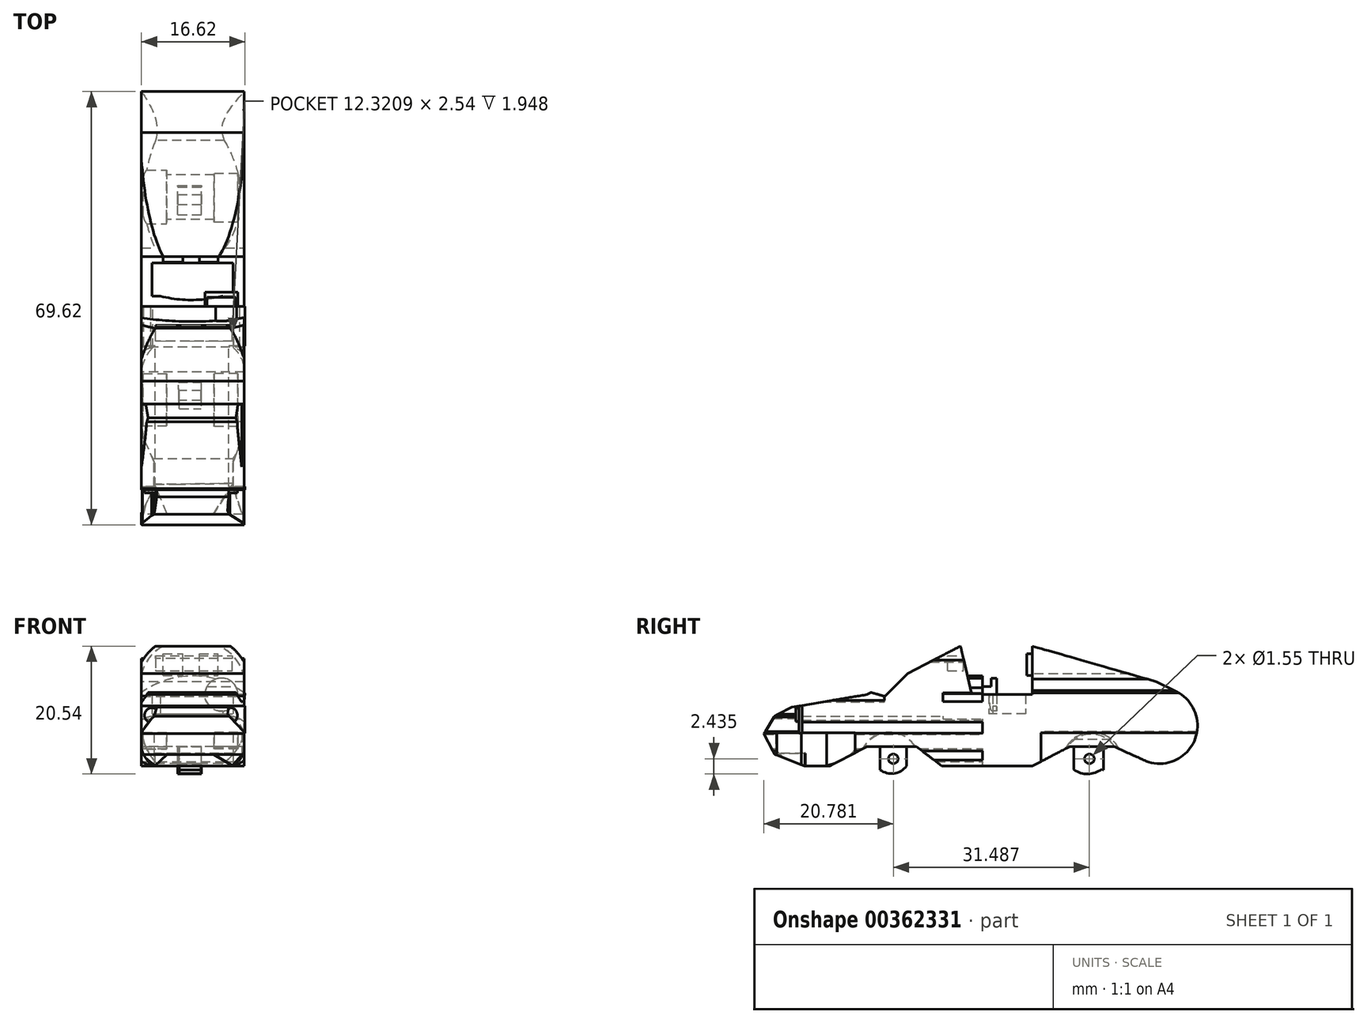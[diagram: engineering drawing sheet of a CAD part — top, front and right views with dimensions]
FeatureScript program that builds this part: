
annotation { "Feature Type Name" : "Feature", "Feature Type Description" : "" }
export const myFeature = defineFeature(function(context is Context, id is Id, definition is map)
    precondition{}
    {
        {
            var Q0;
            Q0=qCreatedBy(makeId("Right.planeOp"),FACE);
            var sketch = newSketch(context, id + "F0", { "sketchPlane" : qUnion([Q0])});
            skArc(sketch, "E0", {"start": v(26.7, 3.42) * mm, "mid": v(34.12, 7.05) * mm, "end": v(31.15, 14.76) * mm});
            skLineSegment(sketch, "E1", {"start": v(31.15, 14.76) * mm, "end": v(27.94, 16.36) * mm});
            skLineSegment(sketch, "E2", {"start": v(27.94, 16.36) * mm, "end": v(8.03, 22.06) * mm});
            skLineSegment(sketch, "E3", {"start": v(8.03, 22.06) * mm, "end": v(8.03, 14.28) * mm});
            skLineSegment(sketch, "E4", {"start": v(8.03, 14.28) * mm, "end": v(-1.74, 14.28) * mm});
            skLineSegment(sketch, "E5", {"start": v(-1.74, 14.28) * mm, "end": v(-3.5, 22.06) * mm});
            skLineSegment(sketch, "E6", {"start": v(-3.5, 22.06) * mm, "end": v(-18.55, 14.28) * mm});
            skLineSegment(sketch, "E7", {"start": v(-18.55, 14.28) * mm, "end": v(-1.74, 14.28) * mm});
            skLineSegment(sketch, "E8", {"start": v(-18.55, 14.28) * mm, "end": v(-30.58, 12.25) * mm});
            skLineSegment(sketch, "E9", {"start": v(-30.58, 12.25) * mm, "end": v(-33.36, 10.81) * mm});
            skLineSegment(sketch, "E10", {"start": v(-33.36, 10.81) * mm, "end": v(-35.08, 7.98) * mm});
            skLineSegment(sketch, "E11", {"start": v(-35.08, 7.98) * mm, "end": v(-33.36, 4.67) * mm});
            skLineSegment(sketch, "E12", {"start": v(-33.36, 4.67) * mm, "end": v(-28.56, 2.8) * mm});
            skLineSegment(sketch, "E13", {"start": v(-28.56, 2.8) * mm, "end": v(-24.5, 2.8) * mm});
            skLineSegment(sketch, "E14", {"start": v(-24.5, 2.8) * mm, "end": v(-18.55, 5.89) * mm});
            skLineSegment(sketch, "E15", {"start": v(-18.55, 5.89) * mm, "end": v(-10.56, 5.89) * mm});
            skLineSegment(sketch, "E16", {"start": v(-10.56, 5.89) * mm, "end": v(-6.5, 2.8) * mm});
            skLineSegment(sketch, "E17", {"start": v(-6.5, 2.8) * mm, "end": v(8.03, 2.8) * mm});
            skLineSegment(sketch, "E18", {"start": v(8.03, 2.8) * mm, "end": v(13.99, 5.89) * mm});
            skLineSegment(sketch, "E19", {"start": v(13.99, 5.89) * mm, "end": v(21.18, 5.89) * mm});
            skLineSegment(sketch, "E20", {"start": v(21.18, 5.89) * mm, "end": v(26.7, 3.42) * mm});
            skSolve(sketch);
        }
        {
            var Q0;
            Q0 = qSketchRegion(id + "F0", true);
            extrude(context, id + "F1", {"entities" : qUnion([Q0]), "depth" : 16.5 * mm});
        }
        {
            var Q0;
            Q0=qCreatedBy(makeId("Top.planeOp"),FACE);
            cPlane(context, id + "F2", {"entities" : qUnion([Q0]), "cplaneType" : CPlaneType.OFFSET, "offset" : 8.38 * mm, "width" : 152.4 * mm, "height" : 152.4 * mm});
        }
        {
            var Q0;
            Q0=qCreatedBy(makeId("Right.planeOp"),FACE);
            cPlane(context, id + "F3", {"entities" : qUnion([Q0]), "cplaneType" : CPlaneType.OFFSET, "offset" : 7.87 * mm, "width" : 152.4 * mm, "height" : 152.4 * mm});
        }
        {
            var Q0;
            Q0=qCreatedBy(makeId("Right.planeOp"),FACE);
            cPlane(context, id + "F4", {"entities" : qUnion([Q0]), "cplaneType" : CPlaneType.OFFSET, "offset" : 11.68 * mm, "width" : 152.4 * mm, "height" : 152.4 * mm});
        }
        {
            var Q0;
            Q0=qCreatedBy(id+"F3.planeOp",FACE);
            cPlane(context, id + "F5", {"entities" : qUnion([Q0]), "cplaneType" : CPlaneType.OFFSET, "offset" : 3.8 * mm, "oppositeDirection" : true, "width" : 152.4 * mm, "height" : 152.4 * mm});
        }
        {
            var Q0;
            Q0=qCreatedBy(id+"F5.planeOp",FACE);
            var sketch = newSketch(context, id + "F6", { "sketchPlane" : qUnion([Q0])});
            skCircle(sketch, "E21", {"center": v(-14.87, 3.35) * mm, "radius": 4.83 * mm});
            skCircle(sketch, "E22", {"center": v(17.63, 3.35) * mm, "radius": 4.84 * mm});
            skSolve(sketch);
        }
        {
            var Q0;
            Q0 = qSketchRegion(id + "F6", true);
            extrude(context, id + "F7", {"entities" : qUnion([Q0]), "operationType" : NewBodyOperationType.REMOVE, "oppositeDirection" : true, "depth" : 3.8 * mm});
        }
        {
            var Q0;
            Q0=qCreatedBy(id+"F4.planeOp",FACE);
            var sketch = newSketch(context, id + "F8", { "sketchPlane" : qUnion([Q0])});
            skCircle(sketch, "E23", {"center": v(-14.9, 3.35) * mm, "radius": 4.87 * mm});
            skCircle(sketch, "E24", {"center": v(17.5, 3.35) * mm, "radius": 4.56 * mm});
            skSolve(sketch);
        }
        {
            var Q0;
            Q0 = qSketchRegion(id + "F8", true);
            extrude(context, id + "F9", {"entities" : qUnion([Q0]), "operationType" : NewBodyOperationType.REMOVE, "depth" : 3.8 * mm});
        }
        {
            var Q0;
            Q0=qCreatedBy(id+"F4.planeOp",FACE);
            cPlane(context, id + "F10", {"entities" : qUnion([Q0]), "cplaneType" : CPlaneType.OFFSET, "offset" : 4.83 * mm, "width" : 152.4 * mm, "height" : 152.4 * mm});
        }
        {
            var Q0;
            Q0=qCreatedBy(makeId("Front.planeOp"),FACE);
            var sketch = newSketch(context, id + "F11", { "sketchPlane" : qUnion([Q0])});
            skArc(sketch, "E25", {"start": v(14.75, 2.9) * mm, "mid": v(16.73, 7.07) * mm, "end": v(14, 10.8) * mm});
            skArc(sketch, "E26", {"start": v(14.75, 2.9) * mm, "mid": v(17.93, 7.19) * mm, "end": v(14, 10.8) * mm});
            skArc(sketch, "E27", {"start": v(2.17, 10.8) * mm, "mid": v(-0.14, 6.94) * mm, "end": v(1.8, 2.9) * mm});
            skArc(sketch, "E28", {"start": v(2.17, 10.8) * mm, "mid": v(-1.78, 7.02) * mm, "end": v(1.8, 2.9) * mm});
            skSolve(sketch);
        }
        {
            var Q0;
            Q0 = qSketchRegion(id + "F11", true);
            extrude(context, id + "F12", {"entities" : qUnion([Q0]), "operationType" : NewBodyOperationType.REMOVE, "depth" : 37.08 * mm});
        }
        {
            var Q0;
            Q0=qCreatedBy(makeId("Top.planeOp"),FACE);
            var sketch = newSketch(context, id + "F13", { "sketchPlane" : qUnion([Q0])});
            skLineSegment(sketch, "E29", {"start": v(0, -33.17) * mm, "end": v(2.02, -29.07) * mm});
            skLineSegment(sketch, "E30", {"start": v(2.02, -29.07) * mm, "end": v(2.02, -24.97) * mm});
            skLineSegment(sketch, "E31", {"start": v(2.02, -24.97) * mm, "end": v(0, -20.42) * mm});
            skLineSegment(sketch, "E32", {"start": v(16.1, -33.14) * mm, "end": v(14.73, -29.07) * mm});
            skLineSegment(sketch, "E33", {"start": v(14.73, -29.07) * mm, "end": v(14.73, -24.97) * mm});
            skLineSegment(sketch, "E34", {"start": v(14.73, -24.97) * mm, "end": v(16.4, -20.42) * mm});
            skLineSegment(sketch, "E35", {"start": v(16.1, -33.14) * mm, "end": v(20.72, -31.59) * mm});
            skLineSegment(sketch, "E36", {"start": v(20.72, -31.59) * mm, "end": v(20.72, -20.2) * mm});
            skLineSegment(sketch, "E37", {"start": v(20.72, -20.2) * mm, "end": v(16.4, -20.42) * mm});
            skLineSegment(sketch, "E38", {"start": v(0, -33.17) * mm, "end": v(-10.4, -33.17) * mm});
            skLineSegment(sketch, "E39", {"start": v(-10.4, -33.17) * mm, "end": v(-6.19, -21.85) * mm});
            skLineSegment(sketch, "E40", {"start": v(-6.19, -21.85) * mm, "end": v(0, -20.42) * mm});
            skSolve(sketch);
        }
        {
            var Q0;
            Q0 = qSketchRegion(id + "F13", true);
            extrude(context, id + "F14", {"entities" : qUnion([Q0]), "operationType" : NewBodyOperationType.REMOVE, "depth" : 8.13 * mm});
        }
        {
            var Q0;
            Q0=qCreatedBy(makeId("Top.planeOp"),FACE);
            var sketch = newSketch(context, id + "F15", { "sketchPlane" : qUnion([Q0])});
            skLineSegment(sketch, "E41", {"start": v(2.13, -28.6) * mm, "end": v(4.1, -33.31) * mm});
            skLineSegment(sketch, "E42", {"start": v(4.1, -33.31) * mm, "end": v(11.56, -33.31) * mm});
            skLineSegment(sketch, "E43", {"start": v(11.56, -33.31) * mm, "end": v(14.75, -28.44) * mm});
            skLineSegment(sketch, "E44", {"start": v(14.75, -28.44) * mm, "end": v(2.13, -28.6) * mm});
            skSolve(sketch);
        }
        {
            var Q0;
            Q0 = qSketchRegion(id + "F15", true);
            extrude(context, id + "F16", {"entities" : qUnion([Q0]), "operationType" : NewBodyOperationType.REMOVE, "depth" : 4.83 * mm});
        }
        {
            var Q0;
            Q0=qCreatedBy(makeId("Front.planeOp"),FACE);
            cPlane(context, id + "F17", {"entities" : qUnion([Q0]), "cplaneType" : CPlaneType.OFFSET, "offset" : 7.11 * mm, "oppositeDirection" : true, "width" : 152.4 * mm, "height" : 152.4 * mm});
        }
        {
            var Q0;
            Q0=qCreatedBy(id+"F17.planeOp",FACE);
            var sketch = newSketch(context, id + "F18", { "sketchPlane" : qUnion([Q0])});
            skArc(sketch, "E45", {"start": v(3.8, 22.2) * mm, "mid": v(0.5, 19.01) * mm, "end": v(0, 14.45) * mm});
            skArc(sketch, "E46", {"start": v(16.43, 14.45) * mm, "mid": v(15.7, 19.17) * mm, "end": v(12.02, 22.2) * mm});
            skLineSegment(sketch, "E47", {"start": v(3.8, 22.2) * mm, "end": v(12.02, 22.2) * mm});
            skArc(sketch, "E48", {"start": v(16.43, 14.45) * mm, "mid": v(8.21, 35.75) * mm, "end": v(0, 14.45) * mm});
            skSolve(sketch);
        }
        {
            var Q0;
            Q0 = qSketchRegion(id + "F18", true);
            extrude(context, id + "F19", {"entities" : qUnion([Q0]), "operationType" : NewBodyOperationType.REMOVE, "oppositeDirection" : true, "depth" : 36.83 * mm});
        }
        {
            var Q0;
            Q0=qCreatedBy(id+"F17.planeOp",FACE);
            var sketch = newSketch(context, id + "F20", { "sketchPlane" : qUnion([Q0])});
            skLineSegment(sketch, "E49.bottom", {"start": v(12.32, 20.84) * mm, "end": v(9.28, 20.84) * mm});
            skLineSegment(sketch, "E49.top", {"start": v(12.32, 17.34) * mm, "end": v(9.28, 17.34) * mm});
            skLineSegment(sketch, "E49.left", {"start": v(12.32, 20.84) * mm, "end": v(12.32, 17.34) * mm});
            skLineSegment(sketch, "E49.right", {"start": v(9.28, 20.84) * mm, "end": v(9.28, 17.34) * mm});
            skPoint(sketch, "E50.firstSnap0", {"position": v(10.8, 20.84) * mm});
            skLineSegment(sketch, "E50.bottom", {"start": v(6.66, 20.84) * mm, "end": v(3.46, 20.84) * mm});
            skLineSegment(sketch, "E50.top", {"start": v(6.66, 17.34) * mm, "end": v(3.46, 17.34) * mm});
            skLineSegment(sketch, "E50.left", {"start": v(6.66, 20.84) * mm, "end": v(6.66, 17.34) * mm});
            skLineSegment(sketch, "E50.right", {"start": v(3.46, 20.84) * mm, "end": v(3.46, 17.34) * mm});
            skSolve(sketch);
        }
        {
            var Q0;
            Q0 = qSketchRegion(id + "F20", true);
            extrude(context, id + "F21", {"entities" : qUnion([Q0]), "operationType" : NewBodyOperationType.ADD, "oppositeDirection" : true, "depth" : 3.8 * mm});
        }
        {
            var Q0;
            Q0=qCreatedBy(makeId("Front.planeOp"),FACE);
            var sketch = newSketch(context, id + "F22", { "sketchPlane" : qUnion([Q0])});
            skArc(sketch, "E51", {"start": v(16.62, 14.45) * mm, "mid": v(8.33, 17.27) * mm, "end": v(0, 14.6) * mm});
            skLineSegment(sketch, "E52", {"start": v(0, 14.6) * mm, "end": v(0, 10.34) * mm});
            skLineSegment(sketch, "E53", {"start": v(0, 10.34) * mm, "end": v(16.28, 10.34) * mm});
            skLineSegment(sketch, "E54", {"start": v(16.28, 10.34) * mm, "end": v(16.62, 14.45) * mm});
            skSolve(sketch);
        }
        {
            var Q0;
            Q0 = qSketchRegion(id + "F22", true);
            extrude(context, id + "F23", {"entities" : qUnion([Q0]), "operationType" : NewBodyOperationType.ADD, "depth" : 6.35 * mm});
        }
        {
            var Q0;
            Q0=qCreatedBy(id+"F2.planeOp",FACE);
            cPlane(context, id + "F24", {"entities" : qUnion([Q0]), "cplaneType" : CPlaneType.OFFSET, "offset" : 2.8 * mm, "width" : 152.4 * mm, "height" : 152.4 * mm});
        }
        {
            var Q0;
            Q0=qCreatedBy(id+"F24.planeOp",FACE);
            var sketch = newSketch(context, id + "F25", { "sketchPlane" : qUnion([Q0])});
            skLineSegment(sketch, "E55.bottom", {"start": v(1.67, 6.97) * mm, "end": v(14.71, 6.97) * mm});
            skLineSegment(sketch, "E55.top", {"start": v(1.67, 1.66) * mm, "end": v(14.71, 1.66) * mm});
            skLineSegment(sketch, "E55.left", {"start": v(1.67, 6.97) * mm, "end": v(1.67, 1.66) * mm});
            skLineSegment(sketch, "E55.right", {"start": v(14.71, 6.97) * mm, "end": v(14.71, 1.66) * mm});
            skArc(sketch, "E56", {"start": v(1.67, 6.97) * mm, "mid": v(2.01, 4.23) * mm, "end": v(3.03, 1.66) * mm});
            skArc(sketch, "E57", {"start": v(13.04, 1.66) * mm, "mid": v(14.28, 4.18) * mm, "end": v(14.71, 6.97) * mm});
            skArc(sketch, "E58", {"start": v(3.03, 1.66) * mm, "mid": v(8.04, 1.05) * mm, "end": v(13.04, 1.66) * mm});
            skSolve(sketch);
        }
        {
            var Q0;
            Q0 = qSketchRegion(id + "F25", true);
            extrude(context, id + "F26", {"entities" : qUnion([Q0]), "operationType" : NewBodyOperationType.REMOVE, "depth" : 4.06 * mm});
        }
        {
            var Q0;
            Q0=qCreatedBy(id+"F17.planeOp",FACE);
            cPlane(context, id + "F27", {"entities" : qUnion([Q0]), "cplaneType" : CPlaneType.OFFSET, "offset" : 10.16 * mm, "width" : 152.4 * mm, "height" : 152.4 * mm});
        }
        {
            var Q0;
            Q0=qCreatedBy(id+"F27.planeOp",FACE);
            var sketch = newSketch(context, id + "F28", { "sketchPlane" : qUnion([Q0])});
            skCircle(sketch, "E59", {"center": v(12.83, 14.27) * mm, "radius": 2.65 * mm});
            skSolve(sketch);
        }
        {
            var Q0;
            Q0 = qSketchRegion(id + "F28", true);
            extrude(context, id + "F29", {"entities" : qUnion([Q0]), "operationType" : NewBodyOperationType.ADD, "oppositeDirection" : true, "depth" : 5.33 * mm});
        }
        {
            var Q0;
            Q0=qCreatedBy(id+"F10.planeOp",FACE);
            var sketch = newSketch(context, id + "F30", { "sketchPlane" : qUnion([Q0])});
            skLineSegment(sketch, "E60.bottom", {"start": v(0, 15.59) * mm, "end": v(1.44, 15.59) * mm});
            skLineSegment(sketch, "E60.top", {"start": v(0, 20.26) * mm, "end": v(1.44, 20.26) * mm});
            skLineSegment(sketch, "E60.left", {"start": v(0, 15.59) * mm, "end": v(0, 20.26) * mm});
            skLineSegment(sketch, "E60.right", {"start": v(1.44, 15.59) * mm, "end": v(1.44, 20.26) * mm});
            skSolve(sketch);
        }
        {
            var Q0;
            Q0 = qSketchRegion(id + "F30", true);
            extrude(context, id + "F31", {"entities" : qUnion([Q0]), "operationType" : NewBodyOperationType.REMOVE, "oppositeDirection" : true, "depth" : 25.4 * mm});
        }
        {
            var Q0;
            Q0=qCreatedBy(id+"F27.planeOp",FACE);
            var sketch = newSketch(context, id + "F32", { "sketchPlane" : qUnion([Q0])});
            skArc(sketch, "E61", {"start": v(16.4, 19.66) * mm, "mid": v(8.16, 24.17) * mm, "end": v(0, 19.51) * mm});
            skArc(sketch, "E62", {"start": v(16.4, 19.66) * mm, "mid": v(8.05, 35.67) * mm, "end": v(0, 19.51) * mm});
            skSolve(sketch);
        }
        {
            var Q0;
            Q0 = qSketchRegion(id + "F32", true);
            extrude(context, id + "F33", {"entities" : qUnion([Q0]), "operationType" : NewBodyOperationType.REMOVE, "depth" : 11.68 * mm});
        }
        {
            var Q0;
            Q0=qCreatedBy(id+"F10.planeOp",FACE);
            var sketch = newSketch(context, id + "F34", { "sketchPlane" : qUnion([Q0])});
            skLineSegment(sketch, "E63", {"start": v(-11.71, 17.95) * mm, "end": v(-15.67, 14) * mm});
            skLineSegment(sketch, "E64", {"start": v(-15.67, 14) * mm, "end": v(-20.53, 15.36) * mm});
            skLineSegment(sketch, "E65", {"start": v(-20.53, 15.36) * mm, "end": v(-11.71, 17.95) * mm});
            skSolve(sketch);
        }
        {
            var Q0;
            Q0 = qSketchRegion(id + "F34", true);
            extrude(context, id + "F35", {"entities" : qUnion([Q0]), "operationType" : NewBodyOperationType.REMOVE, "oppositeDirection" : true, "depth" : 25.4 * mm});
        }
        {
            var Q0;
            Q0=qCreatedBy(id+"F27.planeOp",FACE);
            var sketch = newSketch(context, id + "F36", { "sketchPlane" : qUnion([Q0])});
            skLineSegment(sketch, "E66", {"start": v(14.6, 20.53) * mm, "end": v(2.28, 20.53) * mm});
            skLineSegment(sketch, "E67", {"start": v(2.28, 20.53) * mm, "end": v(2.28, 18.1) * mm});
            skLineSegment(sketch, "E68", {"start": v(2.28, 18.1) * mm, "end": v(14.6, 18.1) * mm});
            skLineSegment(sketch, "E69", {"start": v(14.6, 18.1) * mm, "end": v(14.6, 20.53) * mm});
            skSolve(sketch);
        }
        {
            var Q0;
            Q0 = qSketchRegion(id + "F36", true);
            extrude(context, id + "F37", {"entities" : qUnion([Q0]), "operationType" : NewBodyOperationType.REMOVE, "depth" : 2.54 * mm});
        }
        {
            var Q0;
            Q0=qCreatedBy(makeId("Top.planeOp"),FACE);
            var sketch = newSketch(context, id + "F38", { "sketchPlane" : qUnion([Q0])});
            skLineSegment(sketch, "E70", {"start": v(6.08, -16.43) * mm, "end": v(9.58, -16.43) * mm});
            skLineSegment(sketch, "E71", {"start": v(9.58, -16.43) * mm, "end": v(9.58, -12.17) * mm});
            skLineSegment(sketch, "E72", {"start": v(9.58, -12.17) * mm, "end": v(5.93, -12.17) * mm});
            skLineSegment(sketch, "E73", {"start": v(5.93, -12.17) * mm, "end": v(6.08, -16.43) * mm});
            skSolve(sketch);
        }
        {
            var Q0;
            Q0 = qSketchRegion(id + "F38", true);
            extrude(context, id + "F39", {"entities" : qUnion([Q0]), "operationType" : NewBodyOperationType.ADD, "depth" : 6.35 * mm});
        }
        {
            var Q0;
            Q0=qCreatedBy(id+"F10.planeOp",FACE);
            var sketch = newSketch(context, id + "F40", { "sketchPlane" : qUnion([Q0])});
            skArc(sketch, "E74", {"start": v(-17.03, 2.75) * mm, "mid": v(-14.5, 1.58) * mm, "end": v(-12.07, 2.9) * mm});
            skArc(sketch, "E75", {"start": v(-17.03, 2.75) * mm, "mid": v(-14.35, -3.62) * mm, "end": v(-12.07, 2.9) * mm});
            skSolve(sketch);
        }
        {
            var Q0;
            Q0 = qSketchRegion(id + "F40", true);
            extrude(context, id + "F41", {"entities" : qUnion([Q0]), "operationType" : NewBodyOperationType.REMOVE, "oppositeDirection" : true, "depth" : 25.4 * mm});
        }
        {
            var Q0;
            Q0=qCreatedBy(makeId("Right.planeOp"),FACE);
            var sketch = newSketch(context, id + "F42", { "sketchPlane" : qUnion([Q0])});
            skCircle(sketch, "E76", {"center": v(-14.3, 3.95) * mm, "radius": 0.77 * mm});
            skSolve(sketch);
        }
        {
            var Q0;
            Q0 = qSketchRegion(id + "F42", true);
            extrude(context, id + "F43", {"entities" : qUnion([Q0]), "operationType" : NewBodyOperationType.REMOVE, "depth" : 35.81 * mm});
        }
        {
            var Q0;
            Q0=qCreatedBy(id+"F2.planeOp",FACE);
            var sketch = newSketch(context, id + "F44", { "sketchPlane" : qUnion([Q0])});
            skLineSegment(sketch, "E77.bottom", {"start": v(5.81, 16.57) * mm, "end": v(9.63, 16.57) * mm});
            skLineSegment(sketch, "E77.top", {"start": v(5.81, 19.46) * mm, "end": v(9.63, 19.46) * mm});
            skLineSegment(sketch, "E77.left", {"start": v(5.81, 16.57) * mm, "end": v(5.81, 19.46) * mm});
            skLineSegment(sketch, "E77.right", {"start": v(9.63, 16.57) * mm, "end": v(9.63, 19.46) * mm});
            skPoint(sketch, "E78.oppositeSnap0", {"position": v(9.63, 18.01) * mm});
            skLineSegment(sketch, "E78.top", {"start": v(5.81, 14.71) * mm, "end": v(9.63, 14.71) * mm});
            skLineSegment(sketch, "E78.left", {"start": v(5.81, 16.57) * mm, "end": v(5.81, 14.71) * mm});
            skLineSegment(sketch, "E78.right", {"start": v(9.63, 16.57) * mm, "end": v(9.63, 14.71) * mm});
            skSolve(sketch);
        }
        {
            var Q0;
            Q0 = qSketchRegion(id + "F44", true);
            extrude(context, id + "F45", {"entities" : qUnion([Q0]), "operationType" : NewBodyOperationType.ADD, "oppositeDirection" : true, "depth" : 7.37 * mm});
        }
        {
            var Q0;
            Q0=qCreatedBy(id+"F10.planeOp",FACE);
            var sketch = newSketch(context, id + "F46", { "sketchPlane" : qUnion([Q0])});
            skArc(sketch, "E79", {"start": v(14.6, 2.28) * mm, "mid": v(16.88, 1.52) * mm, "end": v(19.17, 2.28) * mm});
            skArc(sketch, "E80", {"start": v(14.6, 2.28) * mm, "mid": v(16.88, -10.85) * mm, "end": v(19.17, 2.28) * mm});
            skSolve(sketch);
        }
        {
            var Q0;
            Q0 = qSketchRegion(id + "F46", true);
            extrude(context, id + "F47", {"entities" : qUnion([Q0]), "operationType" : NewBodyOperationType.REMOVE, "oppositeDirection" : true, "depth" : 25.4 * mm});
        }
        {
            var Q0;
            Q0=qCreatedBy(id+"F10.planeOp",FACE);
            var sketch = newSketch(context, id + "F48", { "sketchPlane" : qUnion([Q0])});
            skCircle(sketch, "E81", {"center": v(17.19, 3.95) * mm, "radius": 0.78 * mm});
            skSolve(sketch);
        }
        {
            var Q0;
            Q0 = qSketchRegion(id + "F48", true);
            extrude(context, id + "F49", {"entities" : qUnion([Q0]), "operationType" : NewBodyOperationType.REMOVE, "oppositeDirection" : true, "depth" : 25.4 * mm});
        }
        {
            var Q0;
            Q0=qCreatedBy(id+"F17.planeOp",FACE);
            cPlane(context, id + "F50", {"entities" : qUnion([Q0]), "cplaneType" : CPlaneType.OFFSET, "offset" : 2.3 * mm, "oppositeDirection" : true, "width" : 152.4 * mm, "height" : 152.4 * mm});
        }
        {
            var Q0;
            Q0=qCreatedBy(id+"F50.planeOp",FACE);
            var sketch = newSketch(context, id + "F51", { "sketchPlane" : qUnion([Q0])});
            skArc(sketch, "E82", {"start": v(12.52, 2.92) * mm, "mid": v(15.18, 5.25) * mm, "end": v(16.59, 8.5) * mm});
            skArc(sketch, "E83", {"start": v(0, 8.34) * mm, "mid": v(0.9, 5.4) * mm, "end": v(2.74, 2.92) * mm});
            skArc(sketch, "E84", {"start": v(0, 8.34) * mm, "mid": v(-22.04, -6.18) * mm, "end": v(2.74, 2.92) * mm});
            skArc(sketch, "E85", {"start": v(12.52, 2.92) * mm, "mid": v(22.93, -0.4) * mm, "end": v(16.59, 8.5) * mm});
            skSolve(sketch);
        }
        {
            var Q0;
            Q0 = qSketchRegion(id + "F51", true);
            extrude(context, id + "F52", {"entities" : qUnion([Q0]), "operationType" : NewBodyOperationType.REMOVE, "oppositeDirection" : true, "depth" : 25.4 * mm});
        }
        {
            var Q0;
            Q0=qCreatedBy(id+"F27.planeOp",FACE);
            cPlane(context, id + "F53", {"entities" : qUnion([Q0]), "cplaneType" : CPlaneType.OFFSET, "offset" : 26.42 * mm, "width" : 152.4 * mm, "height" : 152.4 * mm});
        }
        {
            var Q0;
            Q0=qCreatedBy(id+"F53.planeOp",FACE);
            var sketch = newSketch(context, id + "F54", { "sketchPlane" : qUnion([Q0])});
            skLineSegment(sketch, "E86", {"start": v(0, 8.21) * mm, "end": v(2.13, 11.1) * mm});
            skLineSegment(sketch, "E87", {"start": v(2.13, 11.1) * mm, "end": v(-11.4, 11.1) * mm});
            skLineSegment(sketch, "E88", {"start": v(-11.4, 11.1) * mm, "end": v(0, 8.21) * mm});
            skLineSegment(sketch, "E89", {"start": v(13.84, 11.1) * mm, "end": v(16.53, 8.21) * mm});
            skLineSegment(sketch, "E90", {"start": v(16.53, 8.21) * mm, "end": v(24.06, 9.86) * mm});
            skLineSegment(sketch, "E91", {"start": v(24.06, 9.86) * mm, "end": v(13.84, 11.1) * mm});
            skLineSegment(sketch, "E92", {"start": v(2.13, 11.1) * mm, "end": v(2.65, 13.15) * mm});
            skLineSegment(sketch, "E93", {"start": v(2.65, 13.15) * mm, "end": v(-11.4, 11.1) * mm});
            skLineSegment(sketch, "E94", {"start": v(13.84, 11.1) * mm, "end": v(14.1, 13.15) * mm});
            skLineSegment(sketch, "E95", {"start": v(14.1, 13.15) * mm, "end": v(24.06, 11.1) * mm});
            skPoint(sketch, "E95.endSnap0", {"position": v(-4.64, 11.1) * mm});
            skLineSegment(sketch, "E96", {"start": v(24.06, 11.1) * mm, "end": v(24.06, 9.86) * mm});
            skSolve(sketch);
        }
        {
            var Q0;
            Q0 = qSketchRegion(id + "F54", true);
            extrude(context, id + "F55", {"entities" : qUnion([Q0]), "operationType" : NewBodyOperationType.REMOVE, "depth" : 28.45 * mm});
        }
        {
            var Q0;
            Q0=qCreatedBy(id+"F53.planeOp",FACE);
            var sketch = newSketch(context, id + "F56", { "sketchPlane" : qUnion([Q0])});
            skLineSegment(sketch, "E97.bottom", {"start": v(0, 12.47) * mm, "end": v(16.58, 12.47) * mm});
            skLineSegment(sketch, "E97.top", {"start": v(0, 8.06) * mm, "end": v(16.58, 8.06) * mm});
            skLineSegment(sketch, "E97.left", {"start": v(0, 12.47) * mm, "end": v(0, 8.06) * mm});
            skLineSegment(sketch, "E97.right", {"start": v(16.58, 12.47) * mm, "end": v(16.58, 8.06) * mm});
            skSolve(sketch);
        }
        {
            var Q0;
            Q0 = qSketchRegion(id + "F56", true);
            extrude(context, id + "F57", {"entities" : qUnion([Q0]), "operationType" : NewBodyOperationType.ADD, "oppositeDirection" : true, "depth" : 0.5 * mm});
        }
        {
            var Q0;
            Q0=qCreatedBy(id+"F53.planeOp",FACE);
            cPlane(context, id + "F58", {"entities" : qUnion([Q0]), "cplaneType" : CPlaneType.OFFSET, "offset" : 13.72 * mm, "oppositeDirection" : true, "width" : 152.4 * mm, "height" : 152.4 * mm});
        }
        {
            var Q0;
            Q0=qCreatedBy(id+"F58.planeOp",FACE);
            var sketch = newSketch(context, id + "F59", { "sketchPlane" : qUnion([Q0])});
            skArc(sketch, "E98", {"start": v(0, 13.06) * mm, "mid": v(1.36, 15.22) * mm, "end": v(2.13, 17.64) * mm});
            skArc(sketch, "E99", {"start": v(14.16, 17.64) * mm, "mid": v(14.87, 15.25) * mm, "end": v(16.1, 13.06) * mm});
            skLineSegment(sketch, "E100", {"start": v(2.13, 17.64) * mm, "end": v(-4.32, 17.64) * mm});
            skLineSegment(sketch, "E101", {"start": v(-4.32, 17.64) * mm, "end": v(0, 13.06) * mm});
            skLineSegment(sketch, "E102", {"start": v(14.16, 17.64) * mm, "end": v(22.91, 17.64) * mm});
            skLineSegment(sketch, "E103", {"start": v(22.91, 17.64) * mm, "end": v(16.1, 13.06) * mm});
            skSolve(sketch);
        }
        {
            var Q0;
            Q0 = qSketchRegion(id + "F59", true);
            extrude(context, id + "F60", {"entities" : qUnion([Q0]), "operationType" : NewBodyOperationType.REMOVE, "depth" : 57.9 * mm});
        }
        {
            var Q0;
            Q0=qCreatedBy(id+"F53.planeOp",FACE);
            var sketch = newSketch(context, id + "F61", { "sketchPlane" : qUnion([Q0])});
            skCircle(sketch, "E104", {"center": v(1.67, 10.95) * mm, "radius": 1.19 * mm});
            skCircle(sketch, "E105", {"center": v(14.15, 10.95) * mm, "radius": 1.25 * mm});
            skSolve(sketch);
        }
        {
            var Q0;
            Q0 = qSketchRegion(id + "F61", true);
            extrude(context, id + "F62", {"entities" : qUnion([Q0]), "operationType" : NewBodyOperationType.ADD, "depth" : 0.5 * mm});
        }
    });
